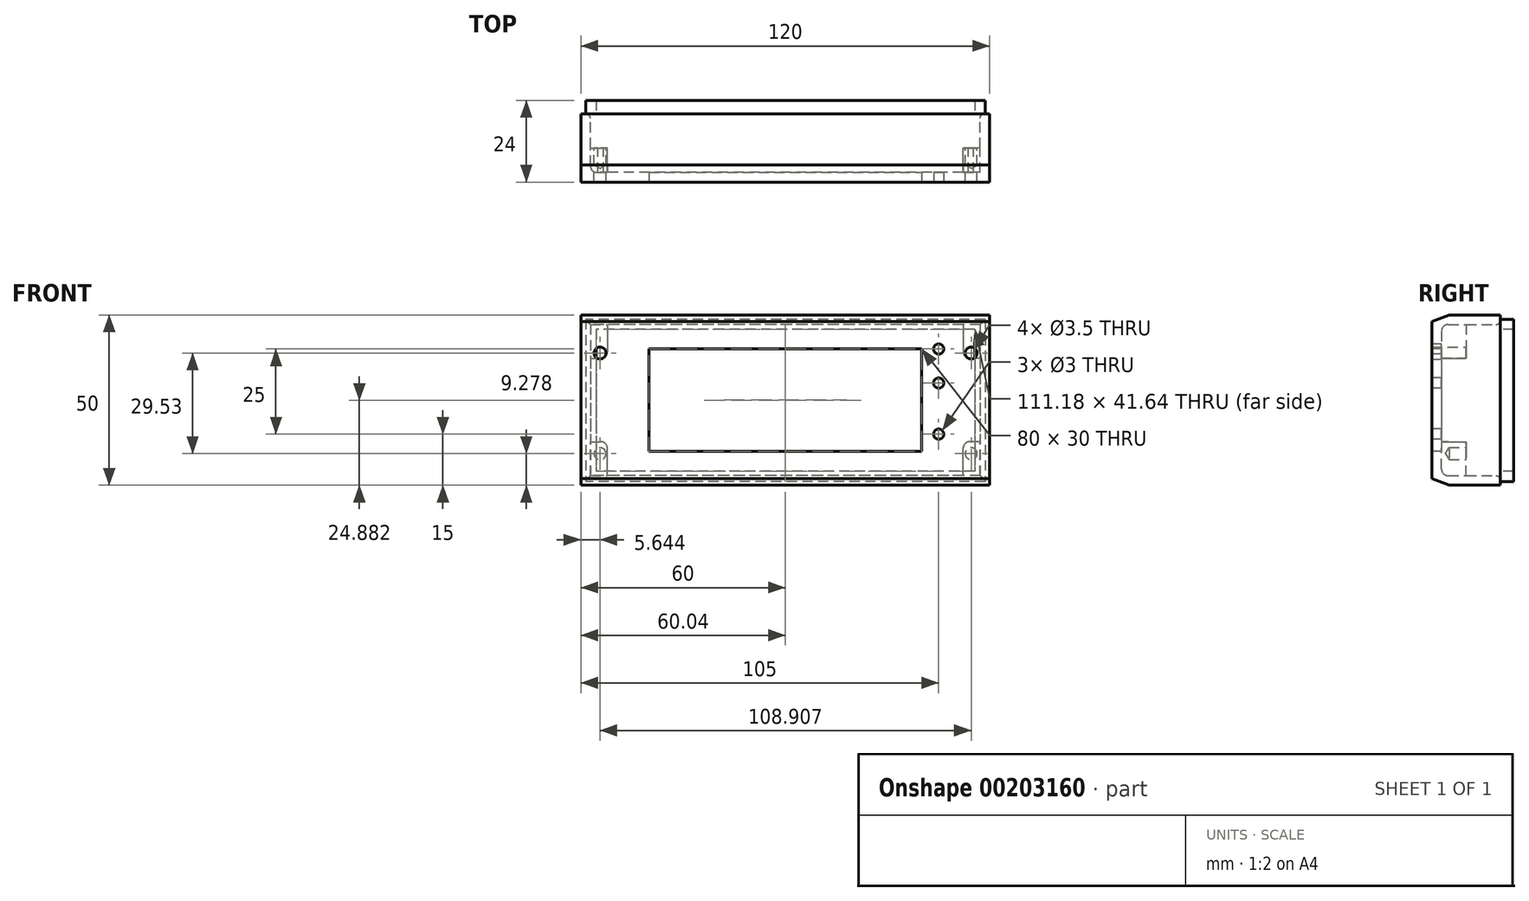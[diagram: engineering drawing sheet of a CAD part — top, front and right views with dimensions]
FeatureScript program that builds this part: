
annotation { "Feature Type Name" : "Feature", "Feature Type Description" : "" }
export const myFeature = defineFeature(function(context is Context, id is Id, definition is map)
    precondition{}
    {
        {
            var Q0;
            Q0=qCreatedBy(makeId("Front.planeOp"),FACE);
            var sketch = newSketch(context, id + "F0", { "sketchPlane" : qUnion([Q0])});
            skLineSegment(sketch, "E0.bottom", {"start": v(60, 25) * mm, "end": v(-60, 25) * mm});
            skLineSegment(sketch, "E0.top", {"start": v(60, -25) * mm, "end": v(-60, -25) * mm});
            skLineSegment(sketch, "E0.left", {"start": v(60, 25) * mm, "end": v(60, -25) * mm});
            skLineSegment(sketch, "E0.right", {"start": v(-60, 25) * mm, "end": v(-60, -25) * mm});
            skPoint(sketch, "E0.middle", {"position": v(0, 0) * mm});
            skSolve(sketch);
        }
        {
            var Q0;
            Q0 = qSketchRegion(id + "F0", true);
            extrude(context, id + "F1", {"entities" : qUnion([Q0]), "depth" : 10 * mm, "hasSecondDirection" : true, "secondDirectionOppositeDirection" : true, "secondDirectionDepth" : 10 * mm});
        }
        {
            var Q0;
            Q0=makeQuery(id+"F1.opExtrude","CAP_FACE",FACE,{"disambiguationData":[OSD([sQuery(id+"F0.wireOp",EDGE,"E0.bottom"),sQuery(id+"F0.wireOp",EDGE,"E0.top"),sQuery(id+"F0.wireOp",EDGE,"E0.left"),sQuery(id+"F0.wireOp",EDGE,"E0.right")])],"isStart":true});
            shell(context, id + "F2", {"entities" : qUnion([Q0]), "thickness" : (7 * 0.4) * mm});
        }
        {
            var Q0;
            Q0=makeQuery(id+"F1.opExtrude","CAP_FACE",FACE,{"disambiguationData":[OSD([sQuery(id+"F0.wireOp",EDGE,"E0.bottom"),sQuery(id+"F0.wireOp",EDGE,"E0.top"),sQuery(id+"F0.wireOp",EDGE,"E0.left"),sQuery(id+"F0.wireOp",EDGE,"E0.right")])],"isStart":false});
            var sketch = newSketch(context, id + "F3", { "sketchPlane" : qUnion([Q0])});
            skLineSegment(sketch, "E1.0", {"start": v(40, -15) * mm, "end": v(40, 15) * mm});
            skLineSegment(sketch, "E1.1", {"start": v(-40, -15) * mm, "end": v(40, -15) * mm});
            skLineSegment(sketch, "E1.2", {"start": v(-40, 15) * mm, "end": v(-40, -15) * mm});
            skLineSegment(sketch, "E1.3", {"start": v(40, 15) * mm, "end": v(-40, 15) * mm});
            skSolve(sketch);
        }
        {
            var Q0;
            Q0 = qSketchRegion(id + "F3", true);
            extrude(context, id + "F4", {"entities" : qUnion([Q0]), "operationType" : NewBodyOperationType.REMOVE, "endBound" : BoundingType.THROUGH_ALL, "oppositeDirection" : true, "depth" : 25.4 * mm});
        }
        {
            var Q0;
            Q0=makeQuery(id+"F1.opExtrude","CAP_FACE",FACE,{"disambiguationData":[OSD([sQuery(id+"F0.wireOp",EDGE,"E0.bottom"),sQuery(id+"F0.wireOp",EDGE,"E0.top"),sQuery(id+"F0.wireOp",EDGE,"E0.left"),sQuery(id+"F0.wireOp",EDGE,"E0.right")])],"isStart":false});
            var sketch = newSketch(context, id + "F5", { "sketchPlane" : qUnion([Q0])});
            skPoint(sketch, "E2", {"position": v(45, 15) * mm});
            skPoint(sketch, "E3", {"position": v(45, 5) * mm});
            skPoint(sketch, "E4", {"position": v(45, -10) * mm});
            skLineSegment(sketch, "E5", {"start": v(45, 0) * mm, "end": v(45, 5) * mm, "construction": true});
            skLineSegment(sketch, "E6", {"start": v(45, 15) * mm, "end": v(45, 5) * mm, "construction": true});
            skLineSegment(sketch, "E7", {"start": v(45, 0) * mm, "end": v(45, -10) * mm, "construction": true});
            skSolve(sketch);
        }
        {
            var Q0;
            Q0=qCreatedBy(makeId("Front.planeOp"),FACE);
            var sketch = newSketch(context, id + "F6", { "sketchPlane" : qUnion([Q0])});
            skLineSegment(sketch, "E8.bottom", {"start": v(57.2, 22.2) * mm, "end": v(52.2, 22.2) * mm});
            skLineSegment(sketch, "E8.top", {"start": v(57.2, 12.2) * mm, "end": v(52.2, 12.2) * mm});
            skLineSegment(sketch, "E8.left", {"start": v(57.2, 22.2) * mm, "end": v(57.2, 12.2) * mm});
            skLineSegment(sketch, "E8.right", {"start": v(52.2, 22.2) * mm, "end": v(52.2, 12.2) * mm});
            skLineSegment(sketch, "E9.bottom", {"start": v(57.2, -22.2) * mm, "end": v(52.2, -22.2) * mm});
            skLineSegment(sketch, "E9.top", {"start": v(57.2, -12.2) * mm, "end": v(52.2, -12.2) * mm});
            skLineSegment(sketch, "E9.left", {"start": v(57.2, -22.2) * mm, "end": v(57.2, -12.2) * mm});
            skLineSegment(sketch, "E9.right", {"start": v(52.2, -22.2) * mm, "end": v(52.2, -12.2) * mm});
            skLineSegment(sketch, "E10.bottom", {"start": v(-57.2, 22.2) * mm, "end": v(-52.2, 22.2) * mm});
            skLineSegment(sketch, "E10.top", {"start": v(-57.2, 12.2) * mm, "end": v(-52.2, 12.2) * mm});
            skLineSegment(sketch, "E10.left", {"start": v(-57.2, 22.2) * mm, "end": v(-57.2, 12.2) * mm});
            skLineSegment(sketch, "E10.right", {"start": v(-52.2, 22.2) * mm, "end": v(-52.2, 12.2) * mm});
            skLineSegment(sketch, "E11.bottom", {"start": v(-57.2, -22.2) * mm, "end": v(-52.2, -22.2) * mm});
            skLineSegment(sketch, "E11.top", {"start": v(-57.2, -12.2) * mm, "end": v(-52.2, -12.2) * mm});
            skLineSegment(sketch, "E11.left", {"start": v(-57.2, -22.2) * mm, "end": v(-57.2, -12.2) * mm});
            skLineSegment(sketch, "E11.right", {"start": v(-52.2, -22.2) * mm, "end": v(-52.2, -12.2) * mm});
            skSolve(sketch);
        }
        {
            var Q0;
            Q0 = qSketchRegion(id + "F6", true);
            extrude(context, id + "F7", {"entities" : qUnion([Q0]), "operationType" : NewBodyOperationType.ADD, "endBound" : BoundingType.UP_TO_NEXT, "depth" : 25 * mm});
        }
        {
            var Q0;
            Q0=makeQuery(id+"F7.opExtrude","SWEPT_EDGE",EDGE,{"disambiguationData":[OSD([sQuery(id+"F6.wireOp",EDGE,"E8.top"),sQuery(id+"F6.wireOp",EDGE,"E8.right")])]});
            var Q1;
            Q1=makeQuery(id+"F7.opExtrude","SWEPT_EDGE",EDGE,{"disambiguationData":[OSD([sQuery(id+"F6.wireOp",EDGE,"E10.top"),sQuery(id+"F6.wireOp",EDGE,"E10.right")])]});
            var Q2;
            Q2=makeQuery(id+"F7.opExtrude","SWEPT_EDGE",EDGE,{"disambiguationData":[OSD([sQuery(id+"F6.wireOp",EDGE,"E11.top"),sQuery(id+"F6.wireOp",EDGE,"E11.right")])]});
            var Q3;
            Q3=makeQuery(id+"F7.opExtrude","SWEPT_EDGE",EDGE,{"disambiguationData":[OSD([sQuery(id+"F6.wireOp",EDGE,"E9.top"),sQuery(id+"F6.wireOp",EDGE,"E9.right")])]});
            var Q4;
            Q4=makeQuery(id+"F7.opExtrude","TWEAK_EDGE",EDGE,{"derivedFrom":[makeQuery(id+"F2.opShell","OFFSET_FACE",FACE,{"disambiguationData":[OSD([sQuery(id+"F0.wireOp",EDGE,"E0.bottom"),sQuery(id+"F0.wireOp",EDGE,"E0.top"),sQuery(id+"F0.wireOp",EDGE,"E0.left"),sQuery(id+"F0.wireOp",EDGE,"E0.right")])]}),makeQuery(id+"F6.imprint","IMPRINT",EDGE,{"derivedFrom":sQuery(id+"F6.wireOp",EDGE,"E9.right")})]});
            var Q5;
            Q5=makeQuery(id+"F7.opExtrude","TWEAK_EDGE",EDGE,{"derivedFrom":[makeQuery(id+"F2.opShell","OFFSET_FACE",FACE,{"disambiguationData":[OSD([sQuery(id+"F0.wireOp",EDGE,"E0.bottom"),sQuery(id+"F0.wireOp",EDGE,"E0.top"),sQuery(id+"F0.wireOp",EDGE,"E0.left"),sQuery(id+"F0.wireOp",EDGE,"E0.right")])]}),makeQuery(id+"F6.imprint","IMPRINT",EDGE,{"derivedFrom":sQuery(id+"F6.wireOp",EDGE,"E8.right")})]});
            var Q6;
            {var subQ0=sQuery(id+"F0.wireOp",EDGE,"E0.bottom");Q6=makeQuery(id+"F2.opShell","OFFSET_EDGE",EDGE,{"disambiguationData":[OSD([subQ0]),TDD([makeQuery(id+"F1.opExtrude","CAP_EDGE",EDGE,{"disambiguationData":[OSD([subQ0])],"isStart":false})])]});}
            var Q7;
            Q7=makeQuery(id+"F7.opExtrude","TWEAK_EDGE",EDGE,{"derivedFrom":[makeQuery(id+"F2.opShell","OFFSET_FACE",FACE,{"disambiguationData":[OSD([sQuery(id+"F0.wireOp",EDGE,"E0.bottom"),sQuery(id+"F0.wireOp",EDGE,"E0.top"),sQuery(id+"F0.wireOp",EDGE,"E0.left"),sQuery(id+"F0.wireOp",EDGE,"E0.right")])]}),makeQuery(id+"F6.imprint","IMPRINT",EDGE,{"derivedFrom":sQuery(id+"F6.wireOp",EDGE,"E10.right")})]});
            var Q8;
            Q8=makeQuery(id+"F7.opExtrude","SWEPT_EDGE",EDGE,{"disambiguationData":[OSD([sQuery(id+"F6.wireOp",EDGE,"E10.bottom"),sQuery(id+"F6.wireOp",EDGE,"E10.right")])]});
            var Q9;
            Q9=makeQuery(id+"F7.opExtrude","SWEPT_EDGE",EDGE,{"disambiguationData":[OSD([sQuery(id+"F6.wireOp",EDGE,"E10.top"),sQuery(id+"F6.wireOp",EDGE,"E10.left")])]});
            var Q10;
            {var subQ0=sQuery(id+"F0.wireOp",EDGE,"E0.right");Q10=makeQuery(id+"F2.opShell","OFFSET_EDGE",EDGE,{"disambiguationData":[OSD([subQ0]),TDD([makeQuery(id+"F1.opExtrude","CAP_EDGE",EDGE,{"disambiguationData":[OSD([subQ0])],"isStart":false})])]});}
            var Q11;
            {var subQ0=sQuery(id+"F0.wireOp",EDGE,"E0.top");Q11=makeQuery(id+"F2.opShell","OFFSET_EDGE",EDGE,{"disambiguationData":[OSD([subQ0]),TDD([makeQuery(id+"F1.opExtrude","CAP_EDGE",EDGE,{"disambiguationData":[OSD([subQ0])],"isStart":false})])]});}
            var Q12;
            Q12=makeQuery(id+"F7.opExtrude","TWEAK_EDGE",EDGE,{"derivedFrom":[makeQuery(id+"F2.opShell","OFFSET_FACE",FACE,{"disambiguationData":[OSD([sQuery(id+"F0.wireOp",EDGE,"E0.bottom"),sQuery(id+"F0.wireOp",EDGE,"E0.top"),sQuery(id+"F0.wireOp",EDGE,"E0.left"),sQuery(id+"F0.wireOp",EDGE,"E0.right")])]}),makeQuery(id+"F6.imprint","IMPRINT",EDGE,{"derivedFrom":sQuery(id+"F6.wireOp",EDGE,"E11.right")})]});
            var Q13;
            Q13=makeQuery(id+"F7.opExtrude","SWEPT_EDGE",EDGE,{"disambiguationData":[OSD([sQuery(id+"F6.wireOp",EDGE,"E11.bottom"),sQuery(id+"F6.wireOp",EDGE,"E11.right")])]});
            fillet(context, id + "F8", {"entities" : qUnion([Q0, Q1, Q2, Q3, Q4, Q5, Q6, Q7, Q8, Q9, Q10, Q11, Q12, Q13]), "radius" : 2 * mm, "tangentPropagation" : true, "allowEdgeOverflow" : false});
        }
        {
            var Q0;
            Q0=makeQuery(id+"F1.opExtrude","CAP_EDGE",EDGE,{"disambiguationData":[OSD([sQuery(id+"F0.wireOp",EDGE,"E0.top")])],"isStart":false});
            var Q1;
            Q1=makeQuery(id+"F1.opExtrude","CAP_EDGE",EDGE,{"disambiguationData":[OSD([sQuery(id+"F0.wireOp",EDGE,"E0.bottom")])],"isStart":false});
            chamfer(context, id + "F9", {"entities" : qUnion([Q0, Q1]), "chamferType" : ChamferType.TWO_OFFSETS, "width1" : 5 * mm, "oppositeDirection" : false, "width2" : 2 * mm, "tangentPropagation" : true});
        }
        {
            var Q0;
            Q0=sQuery(id+"F5.wireOp",VERTEX,"E3");
            var Q1;
            Q1=sQuery(id+"F5.wireOp",VERTEX,"E2");
            var Q2;
            Q2=sQuery(id+"F5.wireOp",VERTEX,"E4");
            var Q3;
            Q3=makeQuery(id+"F1.opExtrude","SWEPT_BODY",BODY,{"disambiguationData":[OSD([sQuery(id+"F0.wireOp",EDGE,"E0.bottom"),sQuery(id+"F0.wireOp",EDGE,"E0.top"),sQuery(id+"F0.wireOp",EDGE,"E0.left"),sQuery(id+"F0.wireOp",EDGE,"E0.right")])]});
            hole(context, id + "F10", {"style" : HoleStyle.SIMPLE, "endStyle" : HoleEndStyle.THROUGH, "holeDiameter" : 3 * mm, "locations" : qUnion([Q0, Q1, Q2]), "scope" : qUnion([Q3]), "isTappedThrough" : true});
        }
        {
            var Q0;
            Q0=qCreatedBy(makeId("Front.planeOp"),FACE);
            var sketch = newSketch(context, id + "F11", { "sketchPlane" : qUnion([Q0])});
            skLineSegment(sketch, "E12.bottom", {"start": v(54.55, 13.8) * mm, "end": v(-54.36, 13.8) * mm, "construction": true});
            skLineSegment(sketch, "E12.top", {"start": v(54.55, -15.72) * mm, "end": v(-54.36, -15.72) * mm, "construction": true});
            skLineSegment(sketch, "E12.left", {"start": v(54.55, 13.8) * mm, "end": v(54.55, -15.72) * mm, "construction": true});
            skLineSegment(sketch, "E12.right", {"start": v(-54.36, 13.8) * mm, "end": v(-54.36, -15.72) * mm, "construction": true});
            skPoint(sketch, "E13", {"position": v(54.55, 13.8) * mm});
            skPoint(sketch, "E14", {"position": v(-54.36, 13.8) * mm});
            skPoint(sketch, "E15", {"position": v(-54.36, -15.72) * mm});
            skPoint(sketch, "E16", {"position": v(54.55, -15.72) * mm});
            skSolve(sketch);
        }
        {
            var Q0;
            Q0=sQuery(id+"F11.wireOp",VERTEX,"E13");
            var Q1;
            Q1=sQuery(id+"F11.wireOp",VERTEX,"E14");
            var Q2;
            Q2=sQuery(id+"F11.wireOp",VERTEX,"E15");
            var Q3;
            Q3=sQuery(id+"F11.wireOp",VERTEX,"E16");
            var Q4;
            Q4=makeQuery(id+"F1.opExtrude","SWEPT_BODY",BODY,{"disambiguationData":[OSD([sQuery(id+"F0.wireOp",EDGE,"E0.bottom"),sQuery(id+"F0.wireOp",EDGE,"E0.top"),sQuery(id+"F0.wireOp",EDGE,"E0.left"),sQuery(id+"F0.wireOp",EDGE,"E0.right")])]});
            hole(context, id + "F12", {"style" : HoleStyle.SIMPLE, "endStyle" : HoleEndStyle.BLIND, "oppositeDirection" : true, "standardTappedOrClearance" : lookupTablePath({ "standard" : "ISO", "engagement" : "25%", "pitch" : "0.75 mm", "size" : "M4", "type" : "Tapped" }), "standardBlindInLast" : lookupTablePath({ "standard" : "ISO", "engagement" : "25%", "pitch" : "0.75 mm", "size" : "M4", "type" : "Tapped" }), "holeDiameter" : 3.5 * mm, "holeDepth" : 5 * mm, "locations" : qUnion([Q0, Q1, Q2, Q3]), "scope" : qUnion([Q4])});
        }
        {
            var Q0;
            Q0=makeQuery(id+"F1.opExtrude","CAP_FACE",FACE,{"disambiguationData":[OSD([sQuery(id+"F0.wireOp",EDGE,"E0.bottom"),sQuery(id+"F0.wireOp",EDGE,"E0.top"),sQuery(id+"F0.wireOp",EDGE,"E0.left"),sQuery(id+"F0.wireOp",EDGE,"E0.right")])],"isStart":true});
            var sketch = newSketch(context, id + "F13", { "sketchPlane" : qUnion([Q0])});
            skLineSegment(sketch, "E17.bottom", {"start": v(-58.63, 23.7) * mm, "end": v(58.55, 23.7) * mm});
            skLineSegment(sketch, "E17.top", {"start": v(-58.63, -23.94) * mm, "end": v(58.55, -23.94) * mm});
            skLineSegment(sketch, "E17.left", {"start": v(-58.63, 23.7) * mm, "end": v(-58.63, -23.94) * mm});
            skLineSegment(sketch, "E17.right", {"start": v(58.55, 23.7) * mm, "end": v(58.55, -23.94) * mm});
            skLineSegment(sketch, "E18.0", {"start": v(-55.63, 20.7) * mm, "end": v(55.55, 20.7) * mm});
            skLineSegment(sketch, "E18.1", {"start": v(-55.63, 20.7) * mm, "end": v(-55.63, -20.94) * mm});
            skLineSegment(sketch, "E18.2", {"start": v(-55.63, -20.94) * mm, "end": v(55.55, -20.94) * mm});
            skLineSegment(sketch, "E18.3", {"start": v(55.55, 20.7) * mm, "end": v(55.55, -20.94) * mm});
            skSolve(sketch);
        }
        {
            var Q0;
            Q0 = qSketchRegion(id + "F13", true);
            extrude(context, id + "F14", {"entities" : qUnion([Q0]), "depth" : 4 * mm});
        }
        {
            var Q0;
            {var subQ0=sQuery(id+"F0.wireOp",EDGE,"E0.bottom");Q0=makeQuery(id+"F2.opShell","OFFSET_EDGE",EDGE,{"disambiguationData":[OSD([subQ0]),TDD([makeQuery(id+"F1.opExtrude","CAP_EDGE",EDGE,{"disambiguationData":[OSD([subQ0])],"isStart":true})])]});}
            var Q1;
            {var subQ0=sQuery(id+"F0.wireOp",EDGE,"E0.right");Q1=makeQuery(id+"F2.opShell","OFFSET_EDGE",EDGE,{"disambiguationData":[OSD([subQ0]),TDD([makeQuery(id+"F1.opExtrude","CAP_EDGE",EDGE,{"disambiguationData":[OSD([subQ0])],"isStart":true})])]});}
            var Q2;
            {var subQ0=sQuery(id+"F0.wireOp",EDGE,"E0.top");Q2=makeQuery(id+"F2.opShell","OFFSET_EDGE",EDGE,{"disambiguationData":[OSD([subQ0]),TDD([makeQuery(id+"F1.opExtrude","CAP_EDGE",EDGE,{"disambiguationData":[OSD([subQ0])],"isStart":true})])]});}
            var Q3;
            {var subQ0=sQuery(id+"F0.wireOp",EDGE,"E0.left");Q3=makeQuery(id+"F2.opShell","OFFSET_EDGE",EDGE,{"disambiguationData":[OSD([subQ0]),TDD([makeQuery(id+"F1.opExtrude","CAP_EDGE",EDGE,{"disambiguationData":[OSD([subQ0])],"isStart":true})])]});}
            fillet(context, id + "F15", {"entities" : qUnion([Q0, Q1, Q2, Q3]), "radius" : 1.2 * mm, "tangentPropagation" : true, "allowEdgeOverflow" : false});
        }
    });
